# Revit family: Door_Entry_FLT-400-FG_Cross-Aluminum
name_source: partatom
category: Doors
units: mm (PartAtom-declared; Revit-internal decimal feet)

## family parameters
Always vertical = Yes
Classification Number = 23.30.10.00
Cut with Voids When Loaded = No
Host = Wall
Room Calculation Point = No
Shared = No

## types (1)
- FLT-400-FG
    Description = ThermaPlank™ Heavy Duty Commercial Entry Doors - FLT-400
    Frame Material = Aluminum
    Function = Interior
    Glass Material = Glass Material
    H1 = 7' - 0"
    Height = 7' - 0"
    Keynote = 08 11 00
    Manufacturer = Cross Aluminum
    Model = FLT-400-FG
    Product Documentation Link = https://www.arcat.com
    Product Page URL = https://www.arcat.com
    Rough Height = 7' - 0"
    Rough Width = 3' - 0"
    Therma Plank Material = Therma Plank
    Thickness = 0' - 0"
    URL = https://www.crossaluminum.com
    W1 = 3' - 0"
    Wall Closure = By host
    Width = 3' - 0"
    Window Height = 5' - 7"

## geometry (parser evidence)
native form markers: Sweep x14
no freeform markers — native parametric forms only
